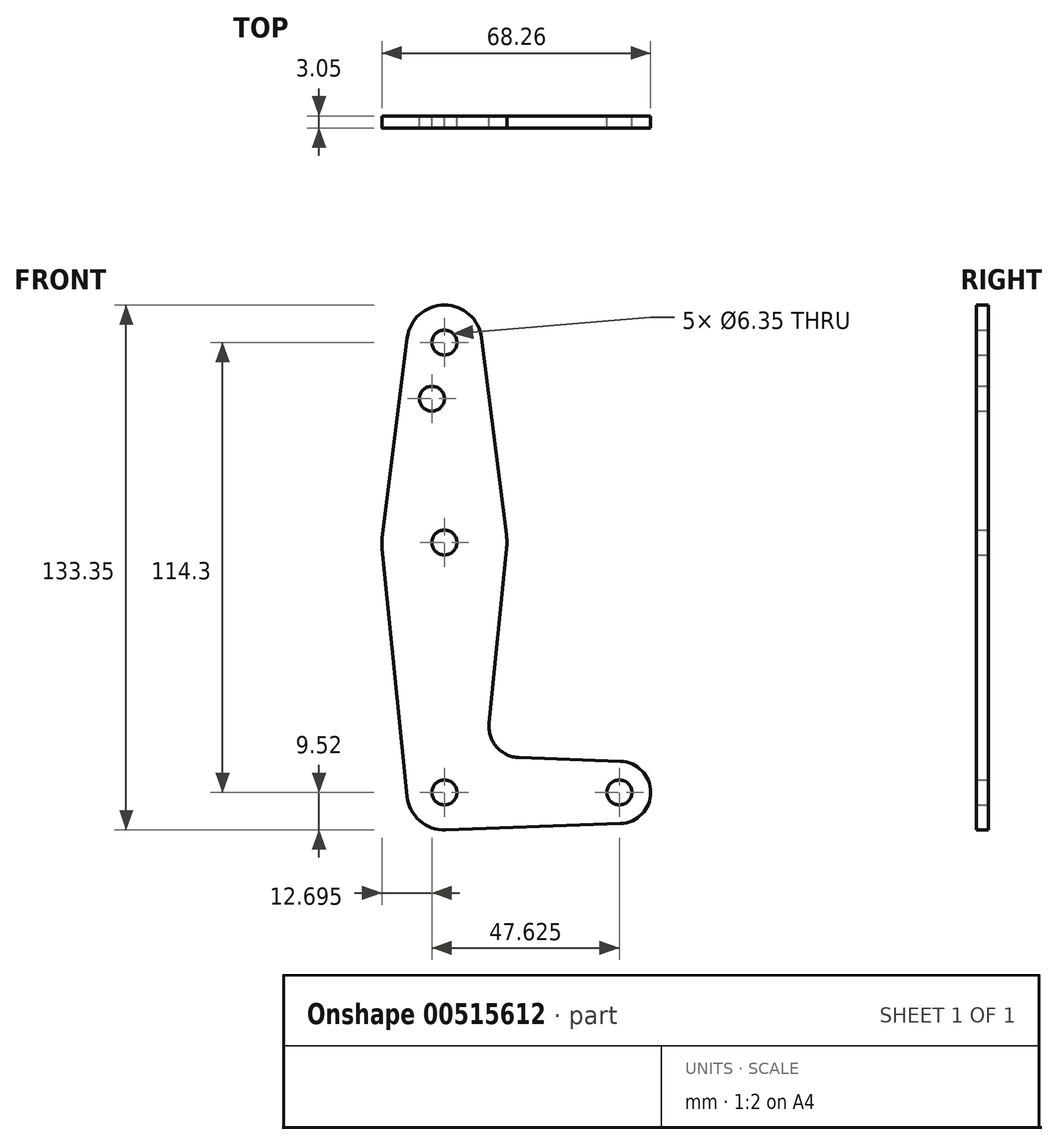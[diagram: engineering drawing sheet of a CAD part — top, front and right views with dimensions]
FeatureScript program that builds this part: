
annotation { "Feature Type Name" : "Feature", "Feature Type Description" : "" }
export const myFeature = defineFeature(function(context is Context, id is Id, definition is map)
    precondition{}
    {
        {
            var Q0;
            Q0=qCreatedBy(makeId("Front.planeOp"),FACE);
            var sketch = newSketch(context, id + "F0", { "sketchPlane" : qUnion([Q0])});
            skCircle(sketch, "E0", {"center": v(0, 0) * mm, "radius": 9.53 * mm});
            skCircle(sketch, "E1", {"center": v(0, 63.5) * mm, "radius": 15.88 * mm});
            skCircle(sketch, "E2", {"center": v(0, 114.3) * mm, "radius": 9.53 * mm});
            skCircle(sketch, "E3", {"center": v(44.45, 0) * mm, "radius": 7.94 * mm});
            skLineSegment(sketch, "E4", {"start": v(0, 0) * mm, "end": v(0, 114.3) * mm, "construction": true});
            skLineSegment(sketch, "E5", {"start": v(0, 0) * mm, "end": v(44.45, 0) * mm, "construction": true});
            skLineSegment(sketch, "E6", {"start": v(-9.45, 115.5) * mm, "end": v(-15.75, 65.48) * mm});
            skLineSegment(sketch, "E7", {"start": v(-15.8, 61.91) * mm, "end": v(-9.48, -0.95) * mm});
            skLineSegment(sketch, "E8", {"start": v(9.45, 115.5) * mm, "end": v(15.75, 65.48) * mm});
            skLineSegment(sketch, "E9", {"start": v(0.34, -9.52) * mm, "end": v(44.73, -7.93) * mm});
            skLineSegment(sketch, "E10", {"start": v(44.73, 7.93) * mm, "end": v(18.97, 8.85) * mm});
            skLineSegment(sketch, "E11", {"start": v(15.8, 61.91) * mm, "end": v(11.34, 17.6) * mm});
            skCircle(sketch, "E12", {"center": v(0, 114.3) * mm, "radius": 3.18 * mm});
            skCircle(sketch, "E13", {"center": v(0, 63.5) * mm, "radius": 3.18 * mm});
            skCircle(sketch, "E14", {"center": v(0, 0) * mm, "radius": 3.18 * mm});
            skCircle(sketch, "E15", {"center": v(44.45, 0) * mm, "radius": 3.18 * mm});
            skCircle(sketch, "E16", {"center": v(-3.18, 100.03) * mm, "radius": 3.18 * mm});
            skArc(sketch, "E17.filletArc", {"start": v(11.34, 17.6) * mm, "mid": v(13.26, 11.57) * mm, "end": v(18.97, 8.85) * mm});
            skSolve(sketch);
        }
        {
            var Q0;
            Q0 = qSketchRegion(id + "F0", true);
            extrude(context, id + "F1", {"entities" : qUnion([Q0]), "depth" : 3.05 * mm});
        }
    });
